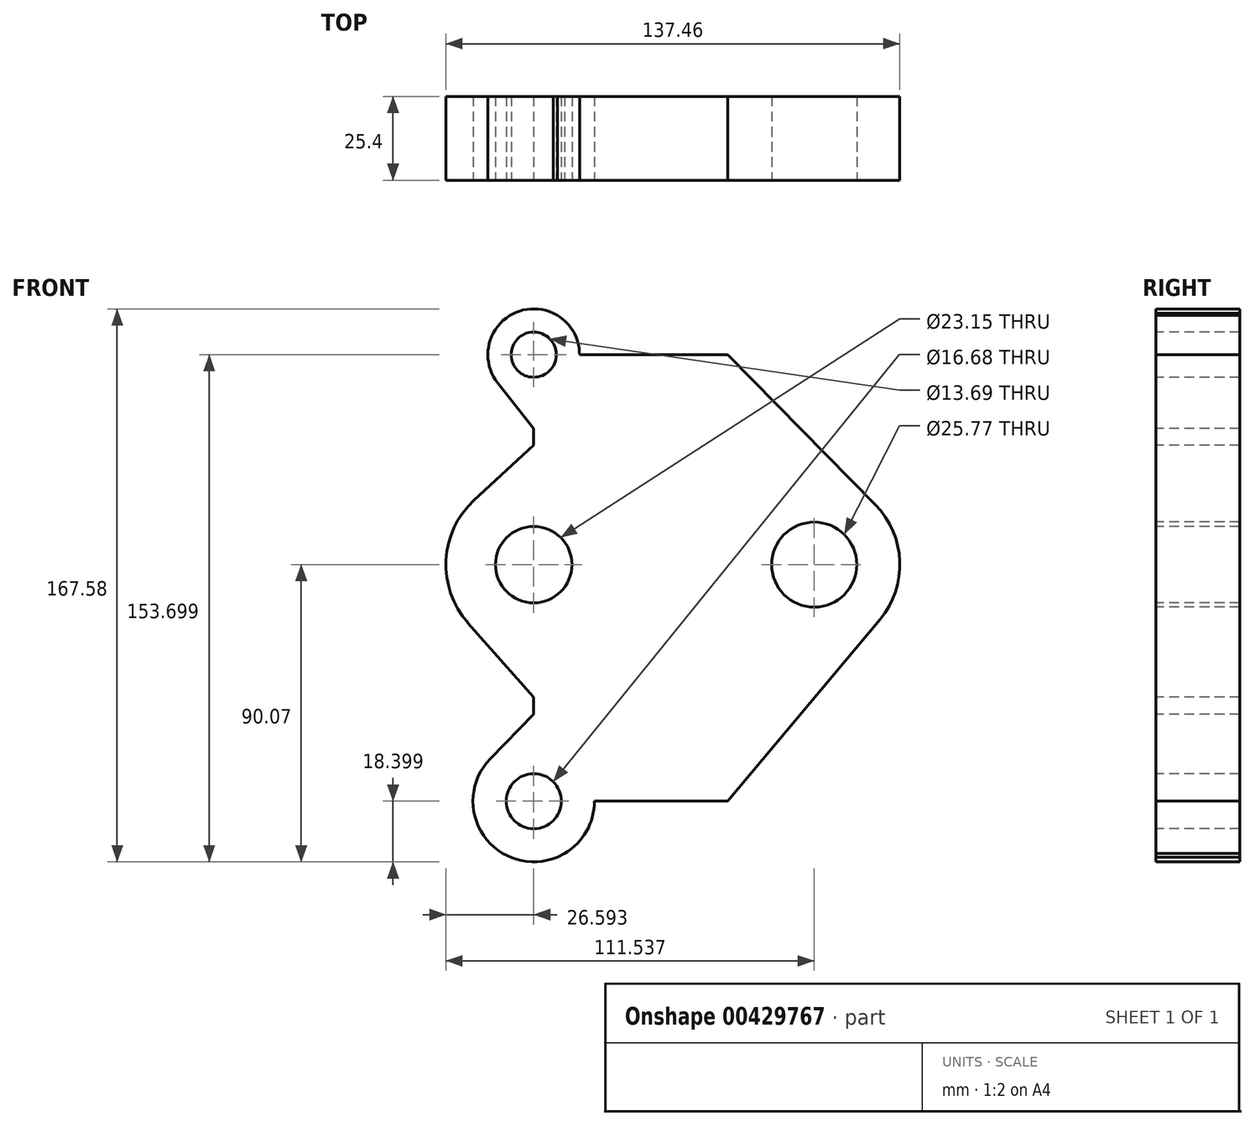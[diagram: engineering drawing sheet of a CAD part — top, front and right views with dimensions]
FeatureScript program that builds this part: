
annotation { "Feature Type Name" : "Feature", "Feature Type Description" : "" }
export const myFeature = defineFeature(function(context is Context, id is Id, definition is map)
    precondition{}
    {
        {
            var Q0;
            Q0=qCreatedBy(makeId("Front.planeOp"),FACE);
            var sketch = newSketch(context, id + "F0", { "sketchPlane" : qUnion([Q0])});
            skCircle(sketch, "E0", {"center": v(16.1, 0) * mm, "radius": 12.88 * mm});
            skCircle(sketch, "E1", {"center": v(16.1, 0) * mm, "radius": 25.92 * mm});
            skCircle(sketch, "E2", {"center": v(-68.85, 63.63) * mm, "radius": 6.84 * mm});
            skCircle(sketch, "E3", {"center": v(-68.85, 63.63) * mm, "radius": 13.88 * mm});
            skCircle(sketch, "E4", {"center": v(-68.85, -71.67) * mm, "radius": 8.34 * mm});
            skCircle(sketch, "E5", {"center": v(-68.85, -71.67) * mm, "radius": 18.4 * mm});
            skCircle(sketch, "E6", {"center": v(-68.85, 0) * mm, "radius": 11.58 * mm});
            skCircle(sketch, "E7", {"center": v(-68.85, 0) * mm, "radius": 26.6 * mm});
            skLineSegment(sketch, "E8", {"start": v(-68.85, 63.63) * mm, "end": v(-68.85, -71.67) * mm});
            skLineSegment(sketch, "E9", {"start": v(-68.85, -71.67) * mm, "end": v(-10.1, -71.67) * mm});
            skLineSegment(sketch, "E10", {"start": v(-10.1, -71.67) * mm, "end": v(-10.1, 63.63) * mm});
            skLineSegment(sketch, "E11", {"start": v(-10.1, 63.63) * mm, "end": v(-68.85, 63.63) * mm});
            skLineSegment(sketch, "E12", {"start": v(-10.1, 63.63) * mm, "end": v(34.58, 18.17) * mm});
            skLineSegment(sketch, "E13", {"start": v(-10.1, -71.67) * mm, "end": v(35.97, -16.64) * mm});
            skLineSegment(sketch, "E14", {"start": v(-61.67, -88.61) * mm, "end": v(-28.16, -71.67) * mm});
            skLineSegment(sketch, "E15", {"start": v(-82, -58.8) * mm, "end": v(-68.85, -45.35) * mm});
            skLineSegment(sketch, "E16", {"start": v(-68.85, -45.35) * mm, "end": v(-68.85, -40.13) * mm});
            skLineSegment(sketch, "E17", {"start": v(-68.85, -40.13) * mm, "end": v(-88.76, -17.62) * mm});
            skLineSegment(sketch, "E18", {"start": v(-68.85, 41.25) * mm, "end": v(-79.74, 55.02) * mm});
            skLineSegment(sketch, "E19", {"start": v(-68.85, 36.16) * mm, "end": v(-86.87, 19.55) * mm});
            skLineSegment(sketch, "E20", {"start": v(-62.96, 76.2) * mm, "end": v(-39.47, 63.63) * mm});
            skSolve(sketch);
        }
        {
            var Q0;
            {var subQ7=sQuery(id+"F0.wireOp",EDGE,"E8");var subQ9=sQuery(id+"F0.wireOp",EDGE,"E2");var subQ10=makeQuery(id+"F0.imprint","INTERSECT",VERTEX,{"derivedFrom":[subQ9,subQ7]});Q0=makeQuery(id+"F0.imprint","IMPRINT",FACE,{"disambiguationData":[TD([[makeQuery(id+"F0.imprint","IMPRINT",EDGE,{"disambiguationData":[TD([[subQ10,1.0]])],"derivedFrom":subQ9}),-1.0]])]});}
            var Q1;
            {var subQ5=sQuery(id+"F0.wireOp",EDGE,"E4");var subQ8=sQuery(id+"F0.wireOp",EDGE,"E8");var subQ11=makeQuery(id+"F0.imprint","INTERSECT",VERTEX,{"derivedFrom":[subQ5,subQ8]});Q1=makeQuery(id+"F0.imprint","IMPRINT",FACE,{"disambiguationData":[TD([[makeQuery(id+"F0.imprint","IMPRINT",EDGE,{"disambiguationData":[TD([[subQ11,-1.0]])],"derivedFrom":subQ5}),-1.0]])]});}
            var Q2;
            {var subQ0=sQuery(id+"F0.wireOp",EDGE,"E8");var subQ1=sQuery(id+"F0.wireOp",EDGE,"E4");var subQ2=makeQuery(id+"F0.imprint","INTERSECT",VERTEX,{"derivedFrom":[subQ1,subQ0]});Q2=makeQuery(id+"F0.imprint","IMPRINT",FACE,{"disambiguationData":[TD([[makeQuery(id+"F0.imprint","IMPRINT",EDGE,{"disambiguationData":[TD([[subQ2,1.0]])],"derivedFrom":subQ1}),-1.0]])]});}
            var Q3;
            {var subQ0=sQuery(id+"F0.wireOp",EDGE,"E8");var subQ1=sQuery(id+"F0.wireOp",EDGE,"E2");var subQ2=makeQuery(id+"F0.imprint","INTERSECT",VERTEX,{"derivedFrom":[subQ1,subQ0]});Q3=makeQuery(id+"F0.imprint","IMPRINT",FACE,{"disambiguationData":[TD([[makeQuery(id+"F0.imprint","IMPRINT",EDGE,{"disambiguationData":[TD([[subQ2,-1.0]])],"derivedFrom":subQ1}),-1.0]])]});}
            var Q4;
            {var subQ0=sQuery(id+"F0.wireOp",EDGE,"E18");Q4=makeQuery(id+"F0.imprint","IMPRINT",FACE,{"disambiguationData":[TD([[makeQuery(id+"F0.imprint","IMPRINT",EDGE,{"derivedFrom":subQ0}),-1.0]])]});}
            var Q5;
            {var subQ0=sQuery(id+"F0.wireOp",EDGE,"E19");Q5=makeQuery(id+"F0.imprint","IMPRINT",FACE,{"disambiguationData":[TD([[makeQuery(id+"F0.imprint","IMPRINT",EDGE,{"derivedFrom":subQ0}),1.0]])]});}
            var Q6;
            {var subQ0=sQuery(id+"F0.wireOp",EDGE,"E17");Q6=makeQuery(id+"F0.imprint","IMPRINT",FACE,{"disambiguationData":[TD([[makeQuery(id+"F0.imprint","IMPRINT",EDGE,{"derivedFrom":subQ0}),-1.0]])]});}
            var Q7;
            {var subQ0=sQuery(id+"F0.wireOp",EDGE,"E15");Q7=makeQuery(id+"F0.imprint","IMPRINT",FACE,{"disambiguationData":[TD([[makeQuery(id+"F0.imprint","IMPRINT",EDGE,{"derivedFrom":subQ0}),-1.0]])]});}
            var Q8;
            {var subQ2=sQuery(id+"F0.wireOp",EDGE,"E8");var subQ6=sQuery(id+"F0.wireOp",EDGE,"E6");var subQ8=makeQuery(id+"F0.imprint","INTERSECT",VERTEX,{"disambiguationData":[OD(0.0)],"derivedFrom":[subQ6,subQ2]});Q8=makeQuery(id+"F0.imprint","IMPRINT",FACE,{"disambiguationData":[TD([[makeQuery(id+"F0.imprint","IMPRINT",EDGE,{"disambiguationData":[TD([[subQ8,-1.0]])],"derivedFrom":subQ6}),-1.0]])]});}
            var Q9;
            {var subQ0=sQuery(id+"F0.wireOp",EDGE,"E8");var subQ1=sQuery(id+"F0.wireOp",EDGE,"E6");var subQ2=makeQuery(id+"F0.imprint","INTERSECT",VERTEX,{"disambiguationData":[OD(0.0)],"derivedFrom":[subQ1,subQ0]});Q9=makeQuery(id+"F0.imprint","IMPRINT",FACE,{"disambiguationData":[TD([[makeQuery(id+"F0.imprint","IMPRINT",EDGE,{"disambiguationData":[TD([[subQ2,1.0]])],"derivedFrom":subQ1}),-1.0]])]});}
            var Q10;
            {var subQ8=sQuery(id+"F0.wireOp",EDGE,"E10");Q10=makeQuery(id+"F0.imprint","IMPRINT",FACE,{"disambiguationData":[TD([[makeQuery(id+"F0.imprint","IMPRINT",EDGE,{"derivedFrom":subQ8}),1.0]])]});}
            var Q11;
            {var subQ0=sQuery(id+"F0.wireOp",EDGE,"E20");var subQ1=sQuery(id+"F0.wireOp",EDGE,"E3");var subQ2=makeQuery(id+"F0.imprint","INTERSECT",VERTEX,{"disambiguationData":[OD(1.0)],"derivedFrom":[subQ1,subQ0]});Q11=makeQuery(id+"F0.imprint","IMPRINT",FACE,{"disambiguationData":[TD([[makeQuery(id+"F0.imprint","IMPRINT",EDGE,{"disambiguationData":[TD([[subQ2,1.0]])],"derivedFrom":subQ1}),-1.0]])]});}
            var Q12;
            {var subQ0=sQuery(id+"F0.wireOp",EDGE,"E14");var subQ1=sQuery(id+"F0.wireOp",EDGE,"E5");var subQ2=makeQuery(id+"F0.imprint","INTERSECT",VERTEX,{"disambiguationData":[OD(1.0)],"derivedFrom":[subQ1,subQ0]});Q12=makeQuery(id+"F0.imprint","IMPRINT",FACE,{"disambiguationData":[TD([[makeQuery(id+"F0.imprint","IMPRINT",EDGE,{"disambiguationData":[TD([[subQ2,-1.0]])],"derivedFrom":subQ1}),-1.0]])]});}
            var Q13;
            Q13=makeQuery(id+"F0.imprint","IMPRINT",FACE,{"disambiguationData":[TD([[makeQuery(id+"F0.imprint","IMPRINT",EDGE,{"derivedFrom":sQuery(id+"F0.wireOp",EDGE,"E10")}),-1.0]])]});
            var Q14;
            Q14=makeQuery(id+"F0.imprint","IMPRINT",FACE,{"disambiguationData":[TD([[makeQuery(id+"F0.imprint","IMPRINT",EDGE,{"derivedFrom":sQuery(id+"F0.wireOp",EDGE,"E0")}),-1.0]])]});
            extrude(context, id + "F1", {"entities" : qUnion([Q0, Q1, Q2, Q3, Q4, Q5, Q6, Q7, Q8, Q9, Q10, Q11, Q12, Q13, Q14]), "oppositeDirection" : true, "depth" : 25.4 * mm});
        }
    });
